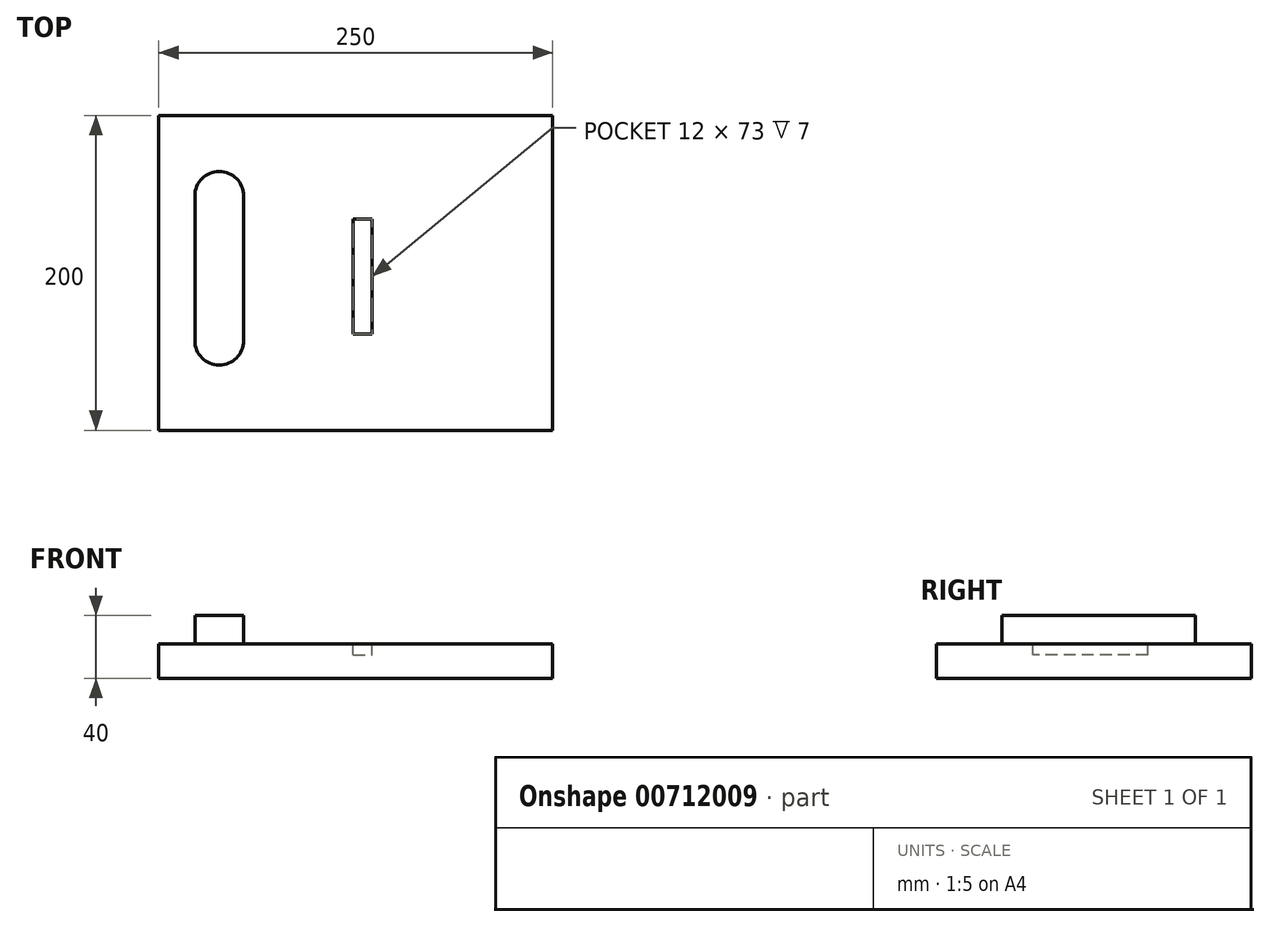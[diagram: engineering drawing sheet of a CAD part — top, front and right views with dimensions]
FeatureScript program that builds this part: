
annotation { "Feature Type Name" : "Feature", "Feature Type Description" : "" }
export const myFeature = defineFeature(function(context is Context, id is Id, definition is map)
    precondition{}
    {
        {
            var Q0;
            Q0=qCreatedBy(makeId("Top.planeOp"),FACE);
            var sketch = newSketch(context, id + "F0", { "sketchPlane" : qUnion([Q0])});
            skLineSegment(sketch, "E0.bottom", {"start": v(76, -86.22) * mm, "end": v(-174, -86.22) * mm});
            skLineSegment(sketch, "E0.top", {"start": v(76, 113.78) * mm, "end": v(-174, 113.78) * mm});
            skLineSegment(sketch, "E0.left", {"start": v(76, -86.22) * mm, "end": v(76, 113.78) * mm});
            skLineSegment(sketch, "E0.right", {"start": v(-174, -86.22) * mm, "end": v(-174, 113.78) * mm});
            skSolve(sketch);
        }
        {
            var Q0;
            Q0=makeQuery(id+"F0.imprint","IMPRINT",FACE,{"disambiguationData":[TD([[makeQuery(id+"F0.imprint","IMPRINT",EDGE,{"derivedFrom":sQuery(id+"F0.wireOp",EDGE,"E0.bottom")}),-1.0]])]});
            extrude(context, id + "F1", {"entities" : qUnion([Q0]), "depth" : 40 * mm, "offsetDistance" : 25 * mm});
        }
        {
            var Q0;
            Q0=makeQuery(id+"F1.opExtrude","CAP_FACE",FACE,{"disambiguationData":[OSD([sQuery(id+"F0.wireOp",EDGE,"E0.bottom"),sQuery(id+"F0.wireOp",EDGE,"E0.top"),sQuery(id+"F0.wireOp",EDGE,"E0.left"),sQuery(id+"F0.wireOp",EDGE,"E0.right")])],"isStart":false});
            var sketch = newSketch(context, id + "F2", { "sketchPlane" : qUnion([Q0])});
            skLineSegment(sketch, "E1", {"start": v(-135.64, -29.2) * mm, "end": v(-135.64, 62.8) * mm});
            skArc(sketch, "E2.0.startCap", {"start": v(-120.14, -29.2) * mm, "mid": v(-135.64, -44.7) * mm, "end": v(-151.14, -29.2) * mm});
            skArc(sketch, "E2.0.endCap", {"start": v(-151.14, 62.8) * mm, "mid": v(-135.64, 78.3) * mm, "end": v(-120.14, 62.8) * mm});
            skLineSegment(sketch, "E2.0.left", {"start": v(-151.14, -29.2) * mm, "end": v(-151.14, 62.8) * mm});
            skLineSegment(sketch, "E2.0.right", {"start": v(-120.14, -29.2) * mm, "end": v(-120.14, 62.8) * mm});
            skSolve(sketch);
        }
        {
            var Q0;
            Q0=makeQuery(id+"F2.imprint","IMPRINT",FACE,{"disambiguationData":[TD([[makeQuery(id+"F2.imprint","IMPRINT",EDGE,{"derivedFrom":sQuery(id+"F2.wireOp",EDGE,"E2.0.startCap")}),-1.0]])]});
            extrude(context, id + "F3", {"entities" : qUnion([Q0]), "operationType" : NewBodyOperationType.REMOVE, "oppositeDirection" : true, "depth" : 18 * mm, "offsetDistance" : 25 * mm});
        }
        {
            var Q0;
            Q0=makeQuery(id+"F1.opExtrude","CAP_FACE",FACE,{"disambiguationData":[OSD([sQuery(id+"F0.wireOp",EDGE,"E0.bottom"),sQuery(id+"F0.wireOp",EDGE,"E0.top"),sQuery(id+"F0.wireOp",EDGE,"E0.left"),sQuery(id+"F0.wireOp",EDGE,"E0.right")])],"isStart":false});
            var sketch = newSketch(context, id + "F4", { "sketchPlane" : qUnion([Q0])});
            skCircle(sketch, "E3", {"center": v(-88.57, 0) * mm, "radius": 21 * mm});
            skSolve(sketch);
        }
        {
            var Q0;
            Q0 = qSketchRegion(id + "F4", true);
            extrude(context, id + "F5", {"entities" : qUnion([Q0]), "operationType" : NewBodyOperationType.REMOVE, "oppositeDirection" : true, "depth" : 10 * mm, "offsetDistance" : 25 * mm});
        }
        {
            var Q0;
            Q0=makeQuery(id+"F1.opExtrude","CAP_FACE",FACE,{"disambiguationData":[OSD([sQuery(id+"F0.wireOp",EDGE,"E0.bottom"),sQuery(id+"F0.wireOp",EDGE,"E0.top"),sQuery(id+"F0.wireOp",EDGE,"E0.left"),sQuery(id+"F0.wireOp",EDGE,"E0.right")])],"isStart":false});
            var sketch = newSketch(context, id + "F6", { "sketchPlane" : qUnion([Q0])});
            skLineSegment(sketch, "E4.bottom", {"start": v(-50.53, 48) * mm, "end": v(-38.53, 48) * mm});
            skLineSegment(sketch, "E4.top", {"start": v(-50.53, -25) * mm, "end": v(-38.53, -25) * mm});
            skLineSegment(sketch, "E4.left", {"start": v(-50.53, 48) * mm, "end": v(-50.53, -25) * mm});
            skLineSegment(sketch, "E4.right", {"start": v(-38.53, 48) * mm, "end": v(-38.53, -25) * mm});
            skSolve(sketch);
        }
        {
            var Q0;
            Q0 = qSketchRegion(id + "F6", true);
            var Q1;
            Q1=makeQuery(id+"F6.imprint","IMPRINT",FACE,{"disambiguationData":[TD([[makeQuery(id+"F6.imprint","IMPRINT",EDGE,{"derivedFrom":sQuery(id+"F6.wireOp",EDGE,"E4.bottom")}),-1.0]])]});
            extrude(context, id + "F7", {"entities" : qUnion([Q0, Q1]), "operationType" : NewBodyOperationType.REMOVE, "oppositeDirection" : true, "depth" : 25 * mm, "offsetDistance" : 25 * mm});
        }
        {
            var Q0;
            Q0=makeQuery(id+"F1.opExtrude","CAP_FACE",FACE,{"disambiguationData":[OSD([sQuery(id+"F0.wireOp",EDGE,"E0.bottom"),sQuery(id+"F0.wireOp",EDGE,"E0.top"),sQuery(id+"F0.wireOp",EDGE,"E0.left"),sQuery(id+"F0.wireOp",EDGE,"E0.right")])],"isStart":false});
            var sketch = newSketch(context, id + "F8", { "sketchPlane" : qUnion([Q0])});
            skLineSegment(sketch, "E5.bottom", {"start": v(-124.65, 109.78) * mm, "end": v(30.35, 109.78) * mm});
            skLineSegment(sketch, "E5.top", {"start": v(-124.65, 94.78) * mm, "end": v(30.35, 94.78) * mm});
            skLineSegment(sketch, "E5.left", {"start": v(-124.65, 109.78) * mm, "end": v(-124.65, 94.78) * mm});
            skLineSegment(sketch, "E5.right", {"start": v(30.35, 109.78) * mm, "end": v(30.35, 94.78) * mm});
            skSolve(sketch);
        }
        {
            var Q0;
            Q0 = qSketchRegion(id + "F8", true);
            extrude(context, id + "F9", {"entities" : qUnion([Q0]), "operationType" : NewBodyOperationType.ADD, "depth" : 25 * mm, "offsetDistance" : 25 * mm});
        }
        {
            var Q0;
            Q0=makeQuery(id+"F9.opExtrude","SWEPT_FACE",FACE,{"disambiguationData":[OSD([sQuery(id+"F8.wireOp",EDGE,"E5.top")])]});
            extrude(context, id + "F10", {"entities" : qUnion([Q0]), "operationType" : NewBodyOperationType.REMOVE, "oppositeDirection" : true, "depth" : 47 * mm, "offsetDistance" : 25 * mm});
        }
    });
